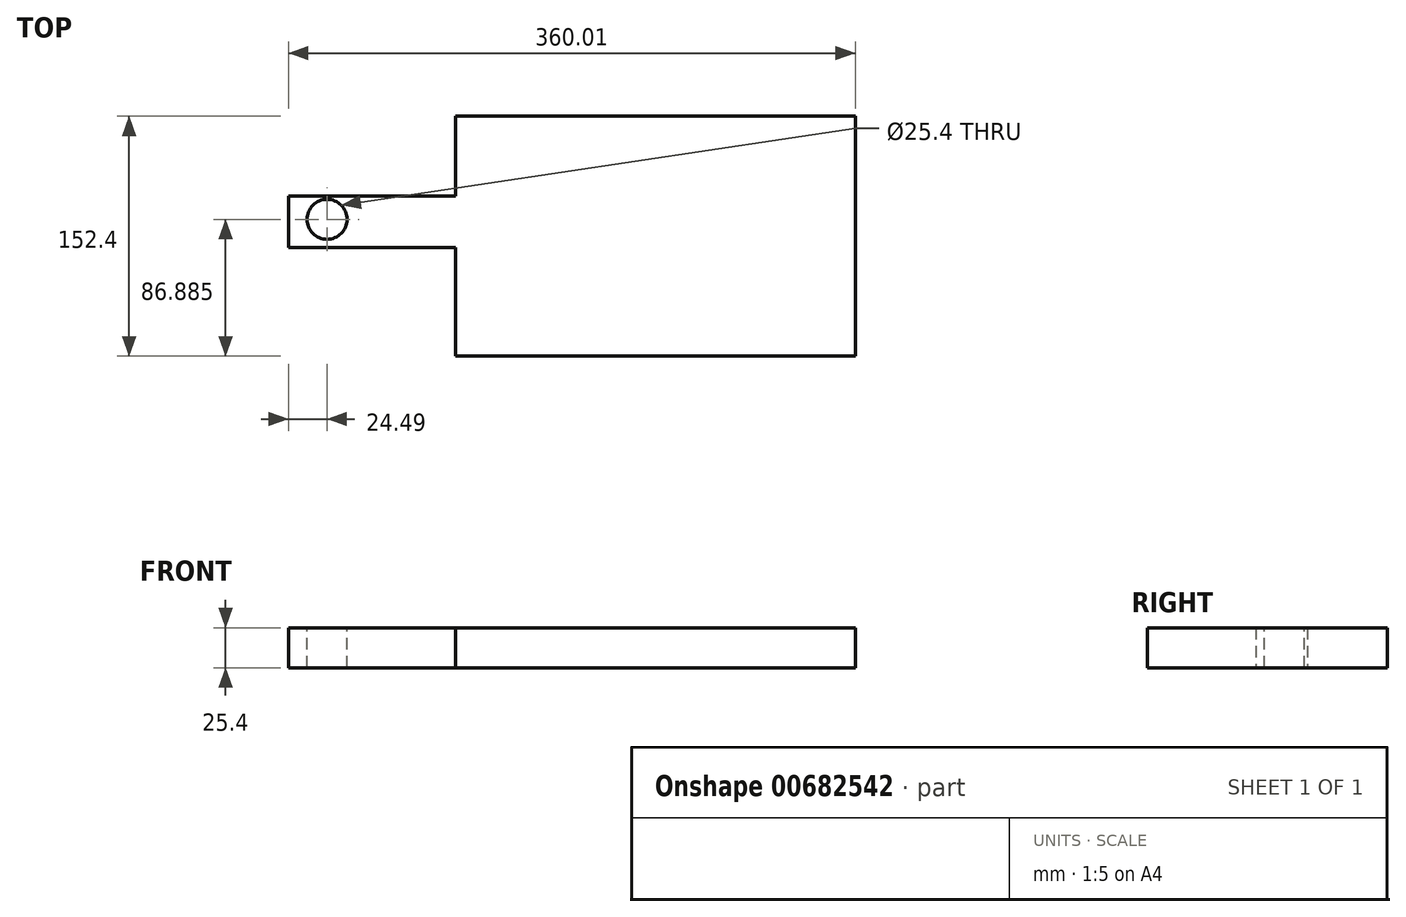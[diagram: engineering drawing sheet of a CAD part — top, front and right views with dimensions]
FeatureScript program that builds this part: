
annotation { "Feature Type Name" : "Feature", "Feature Type Description" : "" }
export const myFeature = defineFeature(function(context is Context, id is Id, definition is map)
    precondition{}
    {
        {
            var Q0;
            Q0=qCreatedBy(makeId("Top.planeOp"),FACE);
            var sketch = newSketch(context, id + "F0", { "sketchPlane" : qUnion([Q0])});
            skLineSegment(sketch, "E0.bottom", {"start": v(0, 0) * mm, "end": v(254, 0) * mm});
            skLineSegment(sketch, "E0.top", {"start": v(0, 152.4) * mm, "end": v(254, 152.4) * mm});
            skLineSegment(sketch, "E0.left", {"start": v(0, 0) * mm, "end": v(0, 152.4) * mm});
            skLineSegment(sketch, "E0.right", {"start": v(254, 0) * mm, "end": v(254, 152.4) * mm});
            skLineSegment(sketch, "E1.bottom", {"start": v(0, 101.6) * mm, "end": v(-106, 101.6) * mm});
            skLineSegment(sketch, "E1.top", {"start": v(0, 69.08) * mm, "end": v(-106, 69.08) * mm});
            skLineSegment(sketch, "E1.left", {"start": v(0, 101.6) * mm, "end": v(0, 69.08) * mm});
            skLineSegment(sketch, "E1.right", {"start": v(-106, 101.6) * mm, "end": v(-106, 69.08) * mm});
            skSolve(sketch);
        }
        {
            var Q0;
            {var subQ3=sQuery(id+"F0.wireOp",EDGE,"E0.bottom");Q0=makeQuery(id+"F0.imprint","IMPRINT",FACE,{"disambiguationData":[TD([[makeQuery(id+"F0.imprint","IMPRINT",EDGE,{"derivedFrom":subQ3}),1.0]])]});}
            var Q1;
            Q1=makeQuery(id+"F0.imprint","IMPRINT",FACE,{"disambiguationData":[TD([[makeQuery(id+"F0.imprint","IMPRINT",EDGE,{"derivedFrom":sQuery(id+"F0.wireOp",EDGE,"E1.bottom")}),1.0]])]});
            extrude(context, id + "F1", {"entities" : qUnion([Q0, Q1]), "depth" : 25.4 * mm, "offsetDistance" : 25.4 * mm});
        }
        {
            var Q0;
            Q0=makeQuery(id+"F1.opExtrude","CAP_FACE",FACE,{"disambiguationData":[OSD([sQuery(id+"F0.wireOp",EDGE,"E0.bottom"),sQuery(id+"F0.wireOp",EDGE,"E0.top"),sQuery(id+"F0.wireOp",EDGE,"E0.left"),sQuery(id+"F0.wireOp",EDGE,"E0.right"),sQuery(id+"F0.wireOp",EDGE,"E1.bottom"),sQuery(id+"F0.wireOp",EDGE,"E1.top"),sQuery(id+"F0.wireOp",EDGE,"E1.right")])],"isStart":false});
            var sketch = newSketch(context, id + "F2", { "sketchPlane" : qUnion([Q0])});
            skCircle(sketch, "E2", {"center": v(-81.52, 86.88) * mm, "radius": 12.7 * mm});
            skSolve(sketch);
        }
        {
            var Q0;
            Q0=makeQuery(id+"F2.imprint","IMPRINT",FACE,{"disambiguationData":[TD([[makeQuery(id+"F2.imprint","IMPRINT",EDGE,{"derivedFrom":sQuery(id+"F2.wireOp",EDGE,"E2")}),1.0]])]});
            extrude(context, id + "F3", {"entities" : qUnion([Q0]), "operationType" : NewBodyOperationType.REMOVE, "oppositeDirection" : true, "depth" : 25.4 * mm, "offsetDistance" : 25.4 * mm});
        }
    });
